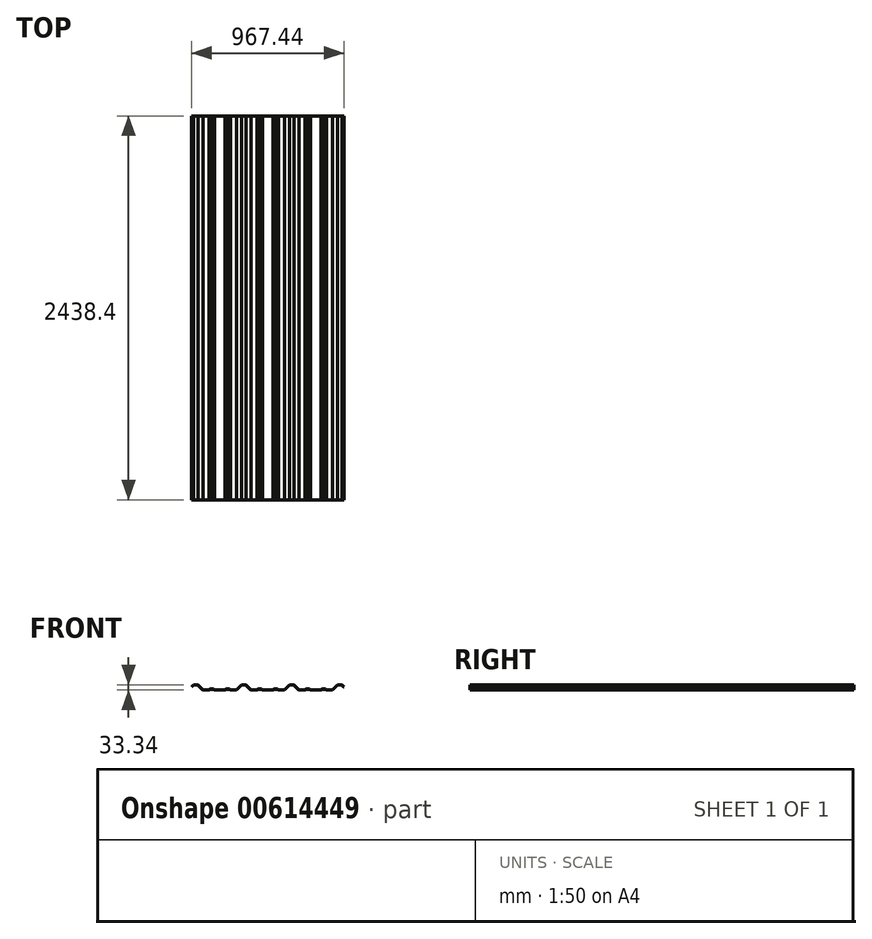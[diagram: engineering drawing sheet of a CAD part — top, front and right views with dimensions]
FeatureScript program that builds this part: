
annotation { "Feature Type Name" : "Feature", "Feature Type Description" : "" }
export const myFeature = defineFeature(function(context is Context, id is Id, definition is map)
    precondition{}
    {
        {
            var Q0;
            Q0=qCreatedBy(makeId("Front.planeOp"),FACE);
            var sketch = newSketch(context, id + "F0", { "sketchPlane" : qUnion([Q0])});
            skLineSegment(sketch, "E0", {"start": v(33.34, 0) * mm, "end": v(-33.34, 0) * mm});
            skLineSegment(sketch, "E1", {"start": v(-33.34, 0) * mm, "end": v(-41.28, 4.76) * mm});
            skLineSegment(sketch, "E2", {"start": v(-41.28, 4.76) * mm, "end": v(-60.32, 4.76) * mm});
            skLineSegment(sketch, "E3", {"start": v(-60.33, 4.76) * mm, "end": v(-68.26, 0) * mm});
            skLineSegment(sketch, "E4", {"start": v(-68.26, 0) * mm, "end": v(-107.95, 0) * mm});
            skLineSegment(sketch, "E5", {"start": v(-107.95, 0) * mm, "end": v(-139.7, 31.75) * mm});
            skLineSegment(sketch, "E6", {"start": v(-139.7, 31.75) * mm, "end": v(-165.1, 31.75) * mm});
            skLineSegment(sketch, "E7", {"start": v(-165.1, 31.75) * mm, "end": v(-196.85, 0) * mm});
            skLineSegment(sketch, "E8", {"start": v(-196.85, 0) * mm, "end": v(-236.54, 0) * mm});
            skLineSegment(sketch, "E9", {"start": v(-236.54, 0) * mm, "end": v(-244.48, 4.76) * mm});
            skLineSegment(sketch, "E10", {"start": v(-244.48, 4.76) * mm, "end": v(-263.53, 4.76) * mm});
            skLineSegment(sketch, "E11", {"start": v(-263.52, 4.76) * mm, "end": v(-271.46, 0) * mm});
            skLineSegment(sketch, "E12", {"start": v(-271.46, 0) * mm, "end": v(-338.14, 0) * mm});
            skLineSegment(sketch, "E13", {"start": v(-338.14, 0) * mm, "end": v(-346.08, 4.76) * mm});
            skLineSegment(sketch, "E14", {"start": v(-346.08, 4.76) * mm, "end": v(-365.13, 4.76) * mm});
            skLineSegment(sketch, "E15", {"start": v(-365.13, 4.76) * mm, "end": v(-373.06, 0) * mm});
            skLineSegment(sketch, "E16", {"start": v(-373.06, 0) * mm, "end": v(-412.75, 0) * mm});
            skLineSegment(sketch, "E17", {"start": v(-412.75, 0) * mm, "end": v(-444.5, 31.75) * mm});
            skLineSegment(sketch, "E18", {"start": v(-444.5, 31.75) * mm, "end": v(-469.9, 31.75) * mm});
            skLineSegment(sketch, "E19", {"start": v(-469.9, 31.75) * mm, "end": v(-482.6, 19.05) * mm});
            skPoint(sketch, "E20", {"position": v(-457.2, 31.75) * mm});
            skPoint(sketch, "E21", {"position": v(-50.8, 4.76) * mm});
            skLineSegment(sketch, "E22", {"start": v(-68.26, 0) * mm, "end": v(-33.34, 0) * mm, "construction": true});
            skLineSegment(sketch, "E23", {"start": v(-50.8, 0) * mm, "end": v(-50.8, 4.76) * mm, "construction": true});
            skLineSegment(sketch, "E24", {"start": v(-196.85, 0) * mm, "end": v(-107.95, 0) * mm, "construction": true});
            skLineSegment(sketch, "E25", {"start": v(-152.4, 0) * mm, "end": v(-152.4, 31.75) * mm, "construction": true});
            skLineSegment(sketch, "E26", {"start": v(-373.06, 0) * mm, "end": v(-338.14, 0) * mm, "construction": true});
            skLineSegment(sketch, "E27", {"start": v(-271.46, 0) * mm, "end": v(-236.54, 0) * mm, "construction": true});
            skLineSegment(sketch, "E28", {"start": v(-254, 0) * mm, "end": v(-254, 4.76) * mm, "construction": true});
            skLineSegment(sketch, "E29", {"start": v(-355.6, 0) * mm, "end": v(-355.6, 4.76) * mm, "construction": true});
            skLineSegment(sketch, "E30", {"start": v(0, 0) * mm, "end": v(0, 148.33) * mm, "construction": true});
            skLineSegment(sketch, "E31.MirrorCS", {"start": v(33.34, 0) * mm, "end": v(41.28, 4.76) * mm});
            skLineSegment(sketch, "E32.MirrorCS", {"start": v(41.28, 4.76) * mm, "end": v(60.32, 4.76) * mm});
            skLineSegment(sketch, "E33.MirrorCS", {"start": v(60.33, 4.76) * mm, "end": v(68.26, 0) * mm});
            skLineSegment(sketch, "E34.MirrorCS", {"start": v(68.26, 0) * mm, "end": v(107.95, 0) * mm});
            skLineSegment(sketch, "E35.MirrorCS", {"start": v(107.95, 0) * mm, "end": v(139.7, 31.75) * mm});
            skLineSegment(sketch, "E36.MirrorCS", {"start": v(139.7, 31.75) * mm, "end": v(165.1, 31.75) * mm});
            skLineSegment(sketch, "E37.MirrorCS", {"start": v(165.1, 31.75) * mm, "end": v(196.85, 0) * mm});
            skLineSegment(sketch, "E38.MirrorCS", {"start": v(196.85, 0) * mm, "end": v(236.54, 0) * mm});
            skLineSegment(sketch, "E39.MirrorCS", {"start": v(236.54, 0) * mm, "end": v(244.48, 4.76) * mm});
            skLineSegment(sketch, "E40.MirrorCS", {"start": v(244.48, 4.76) * mm, "end": v(263.53, 4.76) * mm});
            skLineSegment(sketch, "E41.MirrorCS", {"start": v(263.52, 4.76) * mm, "end": v(271.46, 0) * mm});
            skLineSegment(sketch, "E42.MirrorCS", {"start": v(271.46, 0) * mm, "end": v(338.14, 0) * mm});
            skLineSegment(sketch, "E43.MirrorCS", {"start": v(338.14, 0) * mm, "end": v(346.08, 4.76) * mm});
            skLineSegment(sketch, "E44.MirrorCS", {"start": v(346.08, 4.76) * mm, "end": v(365.13, 4.76) * mm});
            skLineSegment(sketch, "E45.MirrorCS", {"start": v(365.13, 4.76) * mm, "end": v(373.06, 0) * mm});
            skLineSegment(sketch, "E46.MirrorCS", {"start": v(373.06, 0) * mm, "end": v(412.75, 0) * mm});
            skLineSegment(sketch, "E47.MirrorCS", {"start": v(412.75, 0) * mm, "end": v(444.5, 31.75) * mm});
            skLineSegment(sketch, "E48.MirrorCS", {"start": v(444.5, 31.75) * mm, "end": v(469.9, 31.75) * mm});
            skLineSegment(sketch, "E49.MirrorCS", {"start": v(469.9, 31.75) * mm, "end": v(482.6, 19.05) * mm});
            skLineSegment(sketch, "E50.0", {"start": v(-470.56, 33.34) * mm, "end": v(-483.72, 20.17) * mm});
            skLineSegment(sketch, "E50.1", {"start": v(-443.84, 33.34) * mm, "end": v(-470.56, 33.34) * mm});
            skLineSegment(sketch, "E50.2", {"start": v(-412.1, 1.59) * mm, "end": v(-443.84, 33.34) * mm});
            skLineSegment(sketch, "E50.3", {"start": v(-373.5, 1.59) * mm, "end": v(-412.1, 1.59) * mm});
            skLineSegment(sketch, "E50.4", {"start": v(-365.56, 6.35) * mm, "end": v(-373.5, 1.59) * mm});
            skLineSegment(sketch, "E50.5", {"start": v(-345.64, 6.35) * mm, "end": v(-365.56, 6.35) * mm});
            skLineSegment(sketch, "E50.6", {"start": v(-337.7, 1.59) * mm, "end": v(-345.64, 6.35) * mm});
            skLineSegment(sketch, "E50.7", {"start": v(-271.9, 1.59) * mm, "end": v(-337.7, 1.59) * mm});
            skLineSegment(sketch, "E50.8", {"start": v(-263.96, 6.35) * mm, "end": v(-271.9, 1.59) * mm});
            skLineSegment(sketch, "E50.9", {"start": v(-244.04, 6.35) * mm, "end": v(-263.96, 6.35) * mm});
            skLineSegment(sketch, "E50.10", {"start": v(-236.1, 1.59) * mm, "end": v(-244.04, 6.35) * mm});
            skLineSegment(sketch, "E50.11", {"start": v(-197.5, 1.59) * mm, "end": v(-236.1, 1.59) * mm});
            skLineSegment(sketch, "E50.12", {"start": v(-165.76, 33.34) * mm, "end": v(-197.5, 1.59) * mm});
            skLineSegment(sketch, "E50.13", {"start": v(-139.04, 33.34) * mm, "end": v(-165.76, 33.34) * mm});
            skLineSegment(sketch, "E50.14", {"start": v(-107.3, 1.59) * mm, "end": v(-139.04, 33.34) * mm});
            skLineSegment(sketch, "E50.15", {"start": v(-68.7, 1.59) * mm, "end": v(-107.3, 1.59) * mm});
            skLineSegment(sketch, "E50.16", {"start": v(-60.76, 6.35) * mm, "end": v(-68.7, 1.59) * mm});
            skLineSegment(sketch, "E50.17", {"start": v(244.04, 6.35) * mm, "end": v(263.96, 6.35) * mm});
            skLineSegment(sketch, "E50.18", {"start": v(263.96, 6.35) * mm, "end": v(271.9, 1.59) * mm});
            skLineSegment(sketch, "E50.19", {"start": v(271.9, 1.59) * mm, "end": v(337.7, 1.59) * mm});
            skLineSegment(sketch, "E50.20", {"start": v(337.7, 1.59) * mm, "end": v(345.64, 6.35) * mm});
            skLineSegment(sketch, "E50.21", {"start": v(345.64, 6.35) * mm, "end": v(365.56, 6.35) * mm});
            skLineSegment(sketch, "E50.22", {"start": v(365.56, 6.35) * mm, "end": v(373.5, 1.59) * mm});
            skLineSegment(sketch, "E50.23", {"start": v(470.56, 33.34) * mm, "end": v(483.72, 20.17) * mm});
            skLineSegment(sketch, "E50.24", {"start": v(443.84, 33.34) * mm, "end": v(470.56, 33.34) * mm});
            skLineSegment(sketch, "E50.25", {"start": v(412.1, 1.59) * mm, "end": v(443.84, 33.34) * mm});
            skLineSegment(sketch, "E50.26", {"start": v(373.5, 1.59) * mm, "end": v(412.1, 1.59) * mm});
            skLineSegment(sketch, "E50.27", {"start": v(236.1, 1.59) * mm, "end": v(244.04, 6.35) * mm});
            skLineSegment(sketch, "E50.28", {"start": v(197.5, 1.59) * mm, "end": v(236.1, 1.59) * mm});
            skLineSegment(sketch, "E50.29", {"start": v(165.76, 33.34) * mm, "end": v(197.5, 1.59) * mm});
            skLineSegment(sketch, "E50.30", {"start": v(139.04, 33.34) * mm, "end": v(165.76, 33.34) * mm});
            skLineSegment(sketch, "E50.31", {"start": v(107.3, 1.59) * mm, "end": v(139.04, 33.34) * mm});
            skLineSegment(sketch, "E50.32", {"start": v(68.7, 1.59) * mm, "end": v(107.3, 1.59) * mm});
            skLineSegment(sketch, "E50.33", {"start": v(60.76, 6.35) * mm, "end": v(68.7, 1.59) * mm});
            skLineSegment(sketch, "E50.34", {"start": v(40.84, 6.35) * mm, "end": v(60.76, 6.35) * mm});
            skLineSegment(sketch, "E50.35", {"start": v(32.9, 1.59) * mm, "end": v(40.84, 6.35) * mm});
            skLineSegment(sketch, "E50.36", {"start": v(32.9, 1.59) * mm, "end": v(-32.9, 1.59) * mm});
            skLineSegment(sketch, "E50.37", {"start": v(-32.9, 1.59) * mm, "end": v(-40.84, 6.35) * mm});
            skLineSegment(sketch, "E50.38", {"start": v(-40.84, 6.35) * mm, "end": v(-60.76, 6.35) * mm});
            skLineSegment(sketch, "E51", {"start": v(482.6, 19.05) * mm, "end": v(483.72, 20.17) * mm});
            skLineSegment(sketch, "E52", {"start": v(-482.6, 19.05) * mm, "end": v(-483.72, 20.17) * mm});
            skSolve(sketch);
        }
        {
            var Q0;
            Q0 = qSketchRegion(id + "F0", true);
            extrude(context, id + "F1", {"entities" : qUnion([Q0]), "endBound" : BoundingType.SYMMETRIC, "depth" : 2438.4 * mm, "offsetDistance" : 25.4 * mm});
        }
    });
